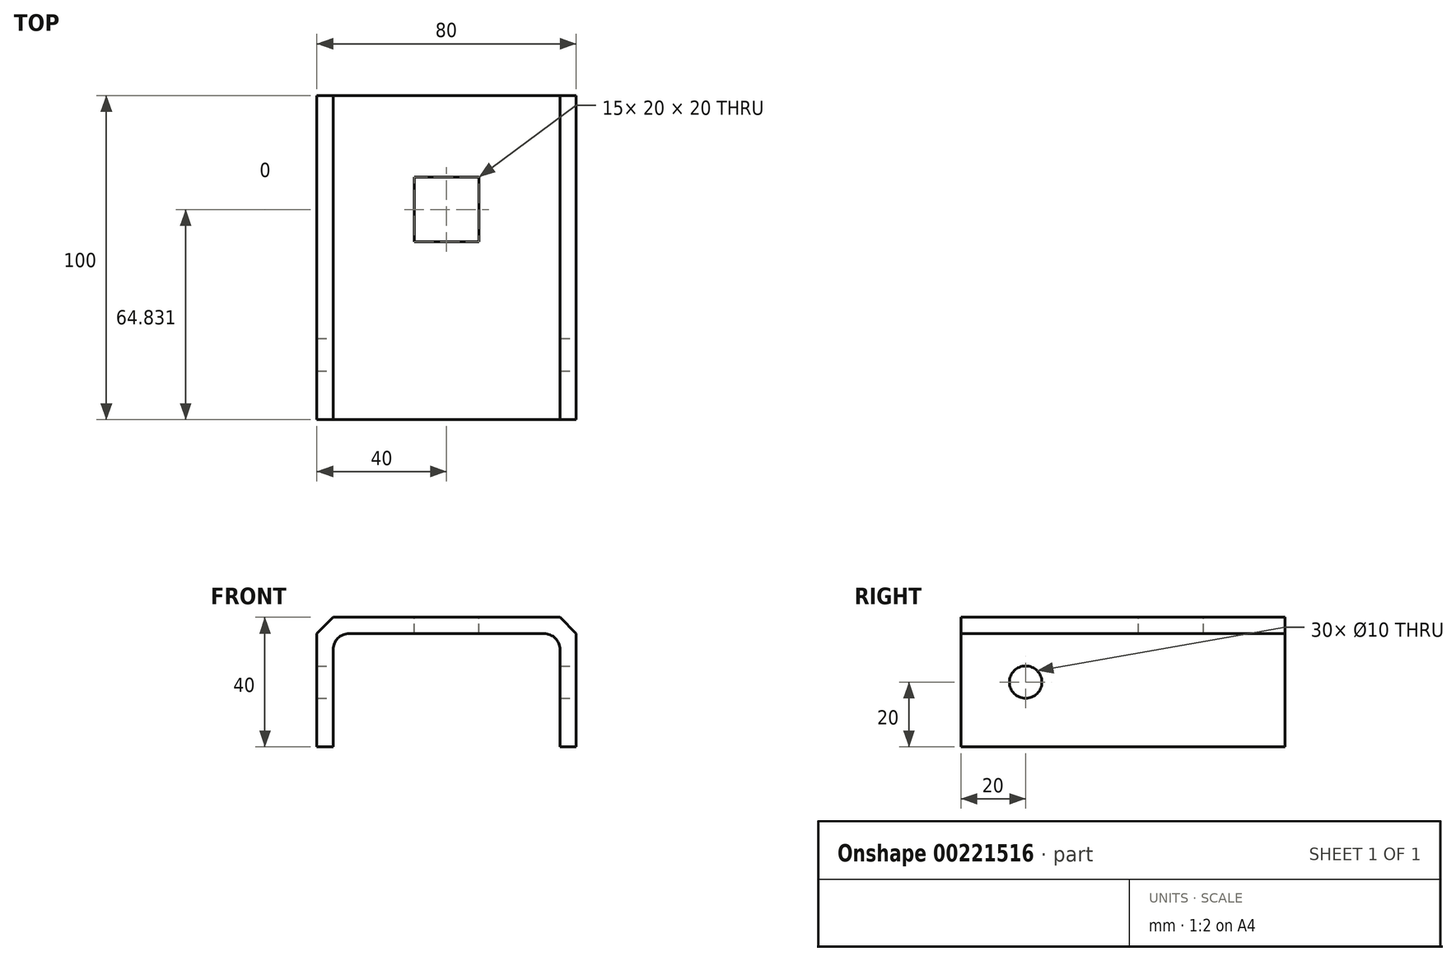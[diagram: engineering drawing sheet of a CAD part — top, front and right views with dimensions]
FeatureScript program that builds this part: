
annotation { "Feature Type Name" : "Feature", "Feature Type Description" : "" }
export const myFeature = defineFeature(function(context is Context, id is Id, definition is map)
    precondition{}
    {
        {
            var Q0;
            Q0=qCreatedBy(makeId("Front.planeOp"),FACE);
            var sketch = newSketch(context, id + "F0", { "sketchPlane" : qUnion([Q0])});
            skLineSegment(sketch, "E0.top", {"start": v(40, 20) * mm, "end": v(-40, 20) * mm});
            skLineSegment(sketch, "E0.left", {"start": v(40, -20) * mm, "end": v(40, 20) * mm});
            skLineSegment(sketch, "E0.right", {"start": v(-40, -20) * mm, "end": v(-40, 20) * mm});
            skPoint(sketch, "E0.middle", {"position": v(0, 0) * mm});
            skLineSegment(sketch, "E1", {"start": v(-40, -20) * mm, "end": v(-35, -20) * mm});
            skLineSegment(sketch, "E2", {"start": v(-35, -20) * mm, "end": v(-35, 10) * mm});
            skLineSegment(sketch, "E3", {"start": v(-30, 15) * mm, "end": v(30, 15) * mm});
            skLineSegment(sketch, "E4", {"start": v(35, 10) * mm, "end": v(35, -20) * mm});
            skLineSegment(sketch, "E5", {"start": v(35, -20) * mm, "end": v(40, -20) * mm});
            skPoint(sketch, "E6.visualSharp", {"position": v(-35, 15) * mm});
            skArc(sketch, "E6.filletArc", {"start": v(-30, 15) * mm, "mid": v(-33.54, 13.54) * mm, "end": v(-35, 10) * mm});
            skPoint(sketch, "E7.visualSharp", {"position": v(35, 15) * mm});
            skArc(sketch, "E7.filletArc", {"start": v(35, 10) * mm, "mid": v(33.54, 13.54) * mm, "end": v(30, 15) * mm});
            skSolve(sketch);
        }
        {
            var Q0;
            Q0=makeQuery(id+"F0.imprint","IMPRINT",FACE,{"disambiguationData":[TD([[makeQuery(id+"F0.imprint","IMPRINT",EDGE,{"derivedFrom":sQuery(id+"F0.wireOp",EDGE,"E0.top")}),1.0]])]});
            extrude(context, id + "F1", {"entities" : qUnion([Q0]), "endBound" : BoundingType.SYMMETRIC, "depth" : 100 * mm});
        }
        {
            var Q0;
            Q0=makeQuery(id+"F1.opExtrude","SWEPT_EDGE",EDGE,{"disambiguationData":[OSD([sQuery(id+"F0.wireOp",EDGE,"E0.top"),sQuery(id+"F0.wireOp",EDGE,"E0.left")])]});
            var Q1;
            Q1=makeQuery(id+"F1.opExtrude","SWEPT_EDGE",EDGE,{"disambiguationData":[OSD([sQuery(id+"F0.wireOp",EDGE,"E0.top"),sQuery(id+"F0.wireOp",EDGE,"E0.right")])]});
            chamfer(context, id + "F2", {"entities" : qUnion([Q0, Q1]), "width" : 5 * mm, "tangentPropagation" : true});
        }
        {
            var Q0;
            Q0=makeQuery(id+"F1.opExtrude","SWEPT_FACE",FACE,{"disambiguationData":[OSD([sQuery(id+"F0.wireOp",EDGE,"E0.top")])]});
            var sketch = newSketch(context, id + "F3", { "sketchPlane" : qUnion([Q0])});
            skLineSegment(sketch, "E8.bottom", {"start": v(10, 24.83) * mm, "end": v(-10, 24.83) * mm});
            skLineSegment(sketch, "E8.top", {"start": v(10, 4.83) * mm, "end": v(-10, 4.83) * mm});
            skLineSegment(sketch, "E8.left", {"start": v(10, 24.83) * mm, "end": v(10, 4.83) * mm});
            skLineSegment(sketch, "E8.right", {"start": v(-10, 24.83) * mm, "end": v(-10, 4.83) * mm});
            skPoint(sketch, "E8.middle", {"position": v(0, 14.83) * mm});
            skSolve(sketch);
        }
        {
            var Q0;
            Q0 = qSketchRegion(id + "F3", true);
            extrude(context, id + "F4", {"entities" : qUnion([Q0]), "operationType" : NewBodyOperationType.REMOVE, "oppositeDirection" : true, "depth" : 10 * mm});
        }
        {
            var Q0;
            Q0=makeQuery(id+"F1.opExtrude","SWEPT_FACE",FACE,{"disambiguationData":[OSD([sQuery(id+"F0.wireOp",EDGE,"E0.left")])]});
            var sketch = newSketch(context, id + "F5", { "sketchPlane" : qUnion([Q0])});
            skCircle(sketch, "E9", {"center": v(-30, 0) * mm, "radius": 5 * mm});
            skSolve(sketch);
        }
        {
            var Q0;
            Q0 = qSketchRegion(id + "F5", true);
            extrude(context, id + "F6", {"entities" : qUnion([Q0]), "operationType" : NewBodyOperationType.REMOVE, "oppositeDirection" : true, "depth" : 100 * mm});
        }
    });
